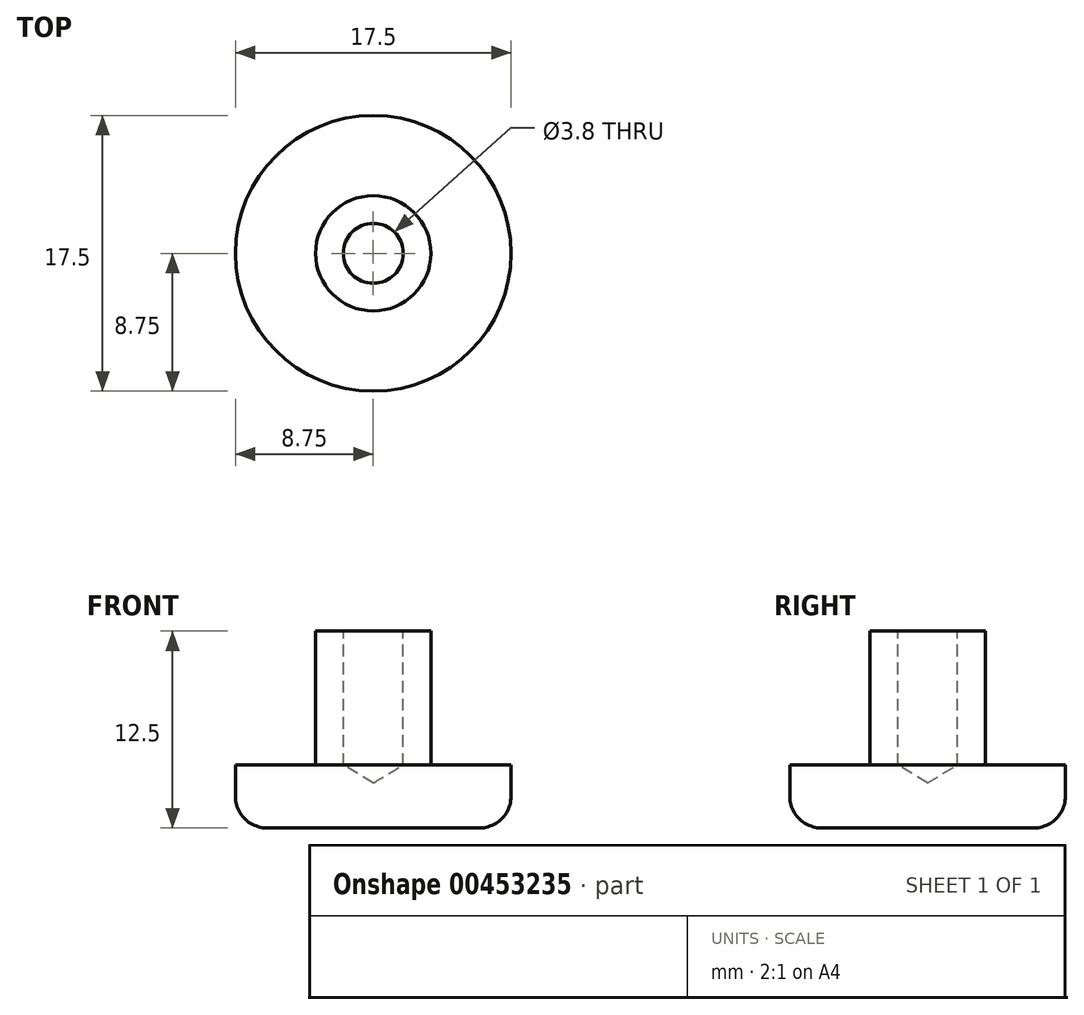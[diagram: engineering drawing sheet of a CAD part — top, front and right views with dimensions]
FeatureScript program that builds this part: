
annotation { "Feature Type Name" : "Feature", "Feature Type Description" : "" }
export const myFeature = defineFeature(function(context is Context, id is Id, definition is map)
    precondition{}
    {
        {
            var Q0;
            Q0=qCreatedBy(makeId("Top.planeOp"),FACE);
            var sketch = newSketch(context, id + "F0", { "sketchPlane" : qUnion([Q0])});
            skCircle(sketch, "E0", {"center": v(0, 0) * mm, "radius": 8.75 * mm});
            skSolve(sketch);
        }
        {
            var Q0;
            Q0=makeQuery(id+"F0.imprint","IMPRINT",FACE,{"disambiguationData":[TD([[makeQuery(id+"F0.imprint","IMPRINT",EDGE,{"derivedFrom":sQuery(id+"F0.wireOp",EDGE,"E0")}),1.0]])]});
            extrude(context, id + "F1", {"entities" : qUnion([Q0]), "depth" : 4 * mm});
        }
        {
            var Q0;
            Q0=makeQuery(id+"F1.opExtrude","CAP_FACE",FACE,{"disambiguationData":[OSD([sQuery(id+"F0.wireOp",EDGE,"E0")])],"isStart":false});
            var sketch = newSketch(context, id + "F2", { "sketchPlane" : qUnion([Q0])});
            skCircle(sketch, "E1", {"center": v(0, 0) * mm, "radius": 3.66 * mm});
            skSolve(sketch);
        }
        {
            var Q0;
            Q0 = qSketchRegion(id + "F2", true);
            extrude(context, id + "F3", {"entities" : qUnion([Q0]), "operationType" : NewBodyOperationType.ADD, "depth" : 8.5 * mm});
        }
        {
            var Q0;
            Q0=makeQuery(id+"F3.opExtrude","CAP_FACE",FACE,{"disambiguationData":[OSD([sQuery(id+"F2.wireOp",EDGE,"E1")])],"isStart":false});
            var sketch = newSketch(context, id + "F4", { "sketchPlane" : qUnion([Q0])});
            skCircle(sketch, "E2", {"center": v(0, 0) * mm, "radius": 2.03 * mm});
            skSolve(sketch);
        }
        {
            var Q0;
            Q0=sQuery(id+"F4.wireOp",VERTEX,"E2.center");
            var Q1;
            Q1=makeQuery(id+"F1.opExtrude","SWEPT_BODY",BODY,{"disambiguationData":[OSD([sQuery(id+"F0.wireOp",EDGE,"E0")])]});
            hole(context, id + "F5", {"style" : HoleStyle.SIMPLE, "endStyle" : HoleEndStyle.BLIND, "standardTappedOrClearance" : lookupTablePath({ "standard" : "ANSI", "engagement" : "75%", "pitch" : "24 tpi", "size" : "#10", "type" : "Tapped" }), "standardBlindInLast" : lookupTablePath({ "standard" : "ANSI", "engagement" : "75%", "pitch" : "24 tpi", "size" : "#10", "type" : "Tapped" }), "holeDiameter" : 3.8 * mm, "showTappedDepth" : true, "holeDepth" : 8.5 * mm, "isTappedThrough" : true, "tappedDepth" : 8.5 * mm, "tapClearance" : 0, "locations" : qUnion([Q0]), "scope" : qUnion([Q1]), "majorDiameter" : 4.83 * mm});
        }
        {
            var Q0;
            Q0=makeQuery(id+"F1.opExtrude","CAP_EDGE",EDGE,{"disambiguationData":[OSD([sQuery(id+"F0.wireOp",EDGE,"E0")])],"isStart":true});
            fillet(context, id + "F6", {"entities" : qUnion([Q0]), "radius" : 2 * mm, "tangentPropagation" : true, "allowEdgeOverflow" : false});
        }
    });
